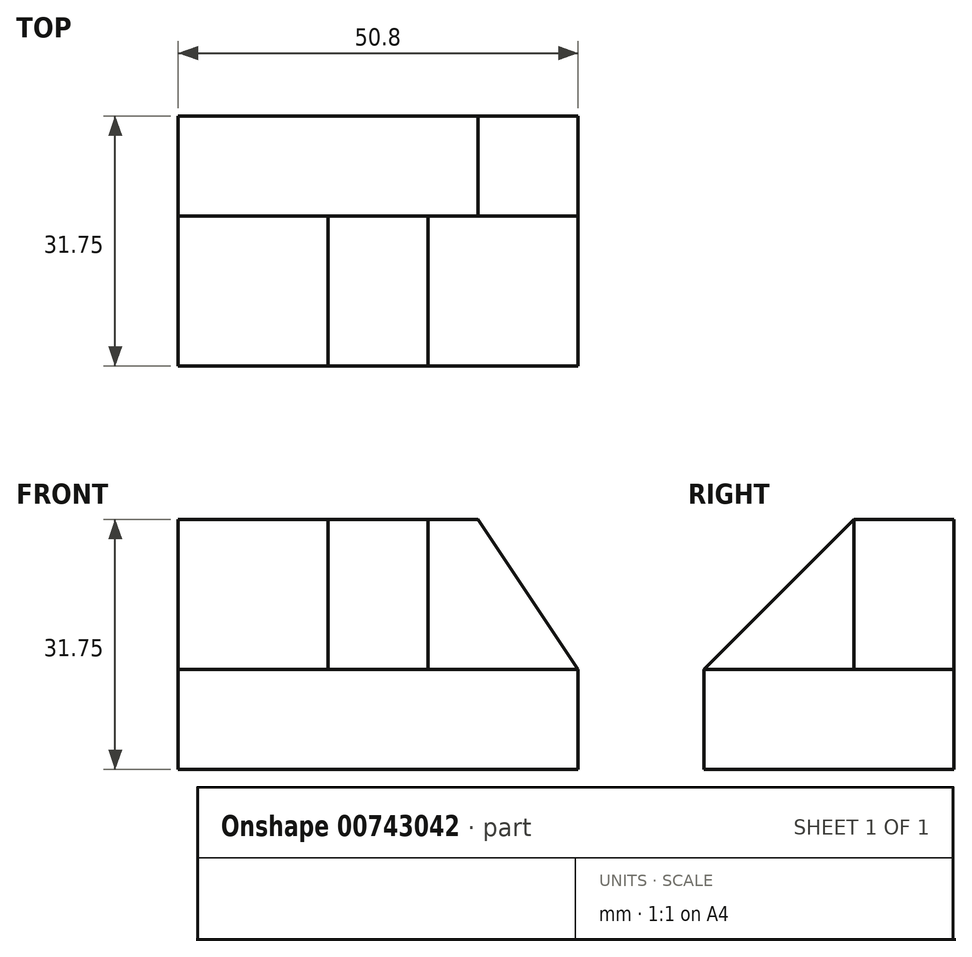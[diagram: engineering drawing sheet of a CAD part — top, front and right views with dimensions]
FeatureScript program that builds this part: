
annotation { "Feature Type Name" : "Feature", "Feature Type Description" : "" }
export const myFeature = defineFeature(function(context is Context, id is Id, definition is map)
    precondition{}
    {
        {
            var Q0;
            Q0=qCreatedBy(makeId("Front.planeOp"),FACE);
            var sketch = newSketch(context, id + "F0", { "sketchPlane" : qUnion([Q0])});
            skLineSegment(sketch, "E0", {"start": v(0, 0) * mm, "end": v(50.8, 0) * mm});
            skLineSegment(sketch, "E1", {"start": v(50.8, 0) * mm, "end": v(50.8, 31.75) * mm});
            skLineSegment(sketch, "E2", {"start": v(50.8, 31.75) * mm, "end": v(0, 31.75) * mm});
            skLineSegment(sketch, "E3", {"start": v(0, 31.75) * mm, "end": v(0, 0) * mm});
            skSolve(sketch);
        }
        {
            var Q0;
            Q0=makeQuery(id+"F0.imprint","IMPRINT",FACE,{"disambiguationData":[TD([[makeQuery(id+"F0.imprint","IMPRINT",EDGE,{"derivedFrom":sQuery(id+"F0.wireOp",EDGE,"E0")}),1.0]])]});
            extrude(context, id + "F1", {"entities" : qUnion([Q0]), "depth" : 31.75 * mm, "offsetDistance" : 25.4 * mm});
        }
        {
            var Q0;
            Q0=makeQuery(id+"F1.opExtrude","SWEPT_FACE",FACE,{"disambiguationData":[OSD([sQuery(id+"F0.wireOp",EDGE,"E1")])]});
            var sketch = newSketch(context, id + "F2", { "sketchPlane" : qUnion([Q0])});
            skLineSegment(sketch, "E4", {"start": v(-31.75, 12.7) * mm, "end": v(-12.7, 12.7) * mm});
            skLineSegment(sketch, "E5", {"start": v(-12.7, 12.7) * mm, "end": v(-12.7, 31.75) * mm});
            skSolve(sketch);
        }
        {
            var Q0;
            {var subQ0=sQuery(id+"F2.wireOp",EDGE,"E4");Q0=makeQuery(id+"F2.imprint","IMPRINT",FACE,{"disambiguationData":[TD([[makeQuery(id+"F2.imprint","IMPRINT",EDGE,{"derivedFrom":subQ0}),1.0]])]});}
            extrude(context, id + "F3", {"entities" : qUnion([Q0]), "operationType" : NewBodyOperationType.REMOVE, "oppositeDirection" : true, "depth" : 19.05 * mm, "offsetDistance" : 25.4 * mm});
        }
        {
            var Q0;
            Q0=makeQuery(id+"F1.opExtrude","SWEPT_FACE",FACE,{"disambiguationData":[OSD([sQuery(id+"F0.wireOp",EDGE,"E3")])]});
            var sketch = newSketch(context, id + "F4", { "sketchPlane" : qUnion([Q0])});
            skLineSegment(sketch, "E6", {"start": v(12.7, 31.75) * mm, "end": v(12.7, 12.7) * mm});
            skLineSegment(sketch, "E7", {"start": v(12.7, 12.7) * mm, "end": v(31.75, 12.7) * mm});
            skSolve(sketch);
        }
        {
            var Q0;
            Q0 = qSketchRegion(id + "F4", true);
            var Q1;
            {var subQ0=sQuery(id+"F4.wireOp",EDGE,"E6");Q1=makeQuery(id+"F4.imprint","IMPRINT",FACE,{"disambiguationData":[TD([[makeQuery(id+"F4.imprint","IMPRINT",EDGE,{"derivedFrom":subQ0}),1.0]])]});}
            extrude(context, id + "F5", {"entities" : qUnion([Q0, Q1]), "operationType" : NewBodyOperationType.REMOVE, "oppositeDirection" : true, "depth" : 19.05 * mm, "offsetDistance" : 25.4 * mm});
        }
        {
            var Q0;
            Q0=makeQuery(id+"F5.boolean.opBoolean","COPY",FACE,{"derivedFrom":makeQuery(id+"F5.opExtrude","CAP_FACE",FACE,{"disambiguationData":[OSD([sQuery(id+"F0.wireOp",EDGE,"E2"),sQuery(id+"F0.wireOp",EDGE,"E3"),sQuery(id+"F4.wireOp",EDGE,"E6"),sQuery(id+"F4.wireOp",EDGE,"E7")])],"isStart":false})});
            var sketch = newSketch(context, id + "F6", { "sketchPlane" : qUnion([Q0])});
            skLineSegment(sketch, "E8", {"start": v(12.7, 31.75) * mm, "end": v(31.75, 12.7) * mm});
            skSolve(sketch);
        }
        {
            var Q0;
            Q0 = qSketchRegion(id + "F6", true);
            var Q1;
            Q1=makeQuery(id+"F6.imprint","IMPRINT",FACE,{"disambiguationData":[TD([[makeQuery(id+"F6.imprint","IMPRINT",EDGE,{"derivedFrom":sQuery(id+"F6.wireOp",EDGE,"E8")}),1.0]])]});
            extrude(context, id + "F7", {"entities" : qUnion([Q0, Q1]), "operationType" : NewBodyOperationType.REMOVE, "oppositeDirection" : true, "depth" : 12.7 * mm, "offsetDistance" : 25.4 * mm});
        }
        {
            var Q0;
            Q0=makeQuery(id+"F3.boolean.opBoolean","COPY",FACE,{"derivedFrom":makeQuery(id+"F3.opExtrude","SWEPT_FACE",FACE,{"disambiguationData":[OSD([sQuery(id+"F2.wireOp",EDGE,"E5")])]})});
            var sketch = newSketch(context, id + "F8", { "sketchPlane" : qUnion([Q0])});
            skLineSegment(sketch, "E9", {"start": v(50.8, 12.7) * mm, "end": v(38.1, 31.75) * mm});
            skSolve(sketch);
        }
        {
            var Q0;
            {var subQ0=sQuery(id+"F8.wireOp",EDGE,"E9");Q0=makeQuery(id+"F8.imprint","IMPRINT",FACE,{"disambiguationData":[TD([[makeQuery(id+"F8.imprint","IMPRINT",EDGE,{"derivedFrom":subQ0}),-1.0]])]});}
            extrude(context, id + "F9", {"entities" : qUnion([Q0]), "operationType" : NewBodyOperationType.REMOVE, "oppositeDirection" : true, "depth" : 12.7 * mm, "offsetDistance" : 25.4 * mm});
        }
    });
